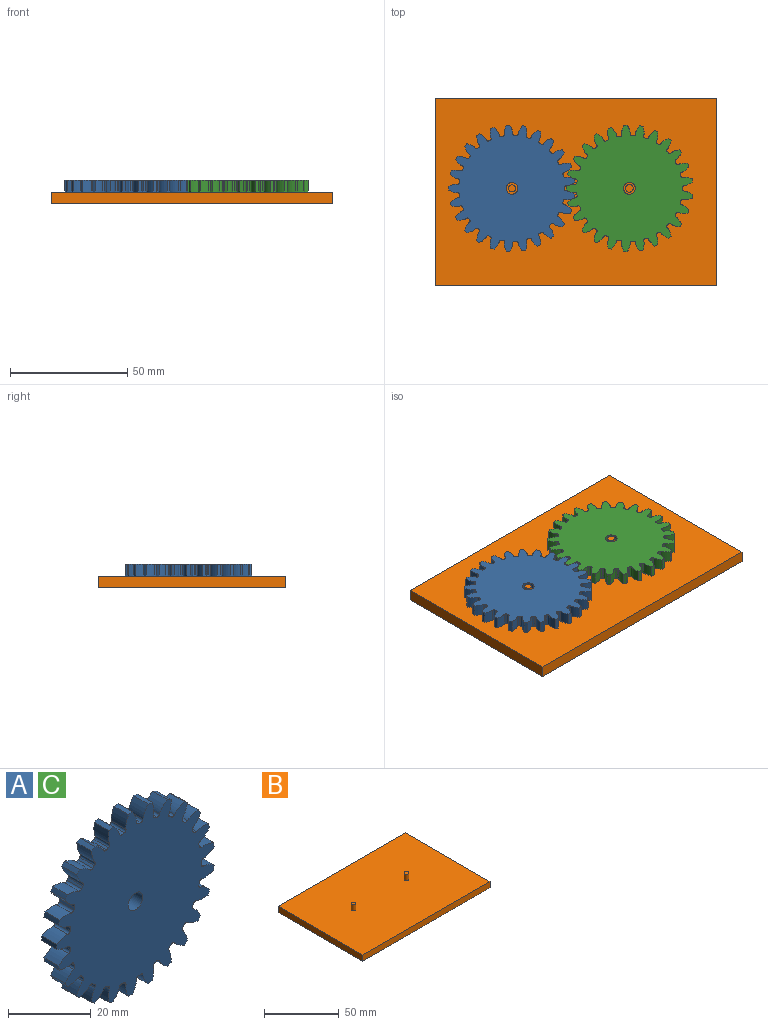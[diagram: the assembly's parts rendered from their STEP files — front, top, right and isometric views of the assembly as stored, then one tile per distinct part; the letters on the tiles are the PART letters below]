
ASSEMBLY  parts=3 mates=2
PART A: 153 faces, bbox 53.9x5x54 mm
  f0: extruded ~5x3.69mm, area 20.3mm2, adj f100,f101,f102,f103
  f1: cylinder r=22.5mm len=5mm, axis (0,1,0), area 3.8mm2, adj f101,f102,f103,f104
  f2: extruded ~5x3.69mm, area 20.3mm2, adj f3,f101,f102,f104
  f3: cylinder r=27mm len=5mm, axis (0,1,0), area 7.2mm2, adj f2,f4,f101,f102
  f4: extruded ~5x3.96mm, area 20.3mm2, adj f3,f101,f102,f105
  f5: cylinder r=22.5mm len=5mm, axis (0,1,0), area 3.8mm2, adj f101,f102,f105,f106
  f6: extruded ~5x3.18mm, area 20.3mm2, adj f7,f101,f102,f106
  f7: cylinder r=27mm len=5mm, axis (0,1,0), area 7.2mm2, adj f6,f8,f101,f102
  f8: extruded ~5x3.98mm, area 20.3mm2, adj f7,f101,f102,f107
  f9: cylinder r=22.5mm len=5mm, axis (0,1,0), area 3.8mm2, adj f101,f102,f107,f108
  f10: extruded ~5x3.14mm, area 20.3mm2, adj f11,f101,f102,f108
  f11: cylinder r=27mm len=5mm, axis (0,1,0), area 7.2mm2, adj f10,f12,f101,f102
  f12: extruded ~5x3.76mm, area 20.3mm2, adj f11,f101,f102,f109
  f13: cylinder r=22.5mm len=5mm, axis (0,1,0), area 3.8mm2, adj f101,f102,f109,f110
  f14: extruded ~5x3.66mm, area 20.3mm2, adj f15,f101,f102,f110
  f15: cylinder r=27mm len=5mm, axis (0,1,0), area 7.2mm2, adj f14,f16,f101,f102
  f16: extruded ~5x3.29mm, area 20.3mm2, adj f15,f101,f102,f111
  f17: cylinder r=22.5mm len=5mm, axis (0,1,0), area 3.8mm2, adj f101,f102,f111,f112
  f18: extruded ~5x3.95mm, area 20.3mm2, adj f19,f101,f102,f112
  f19: cylinder r=27mm len=5mm, axis (0,1,0), area 7.2mm2, adj f18,f20,f101,f102
  f20: extruded ~5x3.03mm, area 20.3mm2, adj f19,f101,f102,f113
  f21: cylinder r=22.5mm len=5mm, axis (0,1,0), area 3.8mm2, adj f101,f102,f113,f114
  f22: extruded ~5x3.99mm, area 20.3mm2, adj f23,f101,f102,f114
  f23: cylinder r=27mm len=5mm, axis (0,1,0), area 7.2mm2, adj f22,f24,f101,f102
  f24: extruded ~5x3.58mm, area 20.3mm2, adj f23,f101,f102,f115
  f25: cylinder r=22.5mm len=5mm, axis (0,1,0), area 3.8mm2, adj f101,f102,f115,f116
  f26: extruded ~5x3.78mm, area 20.3mm2, adj f27,f101,f102,f116
  f27: cylinder r=27mm len=5mm, axis (0,1,0), area 7.2mm2, adj f26,f28,f101,f102
  f28: extruded ~5x3.91mm, area 20.3mm2, adj f27,f101,f102,f117
  f29: cylinder r=22.5mm len=5mm, axis (0,1,0), area 3.8mm2, adj f101,f102,f117,f118
  f30: extruded ~5x3.33mm, area 20.3mm2, adj f31,f101,f102,f118
  f31: cylinder r=27mm len=5mm, axis (0,1,0), area 7.2mm2, adj f30,f32,f101,f102
  f32: extruded ~5x4mm, area 20.3mm2, adj f31,f101,f102,f119
  f33: cylinder r=22.5mm len=5mm, axis (0,1,0), area 3.8mm2, adj f101,f102,f119,f120
  f34: extruded ~5x2.98mm, area 20.3mm2, adj f35,f101,f102,f120
  f35: cylinder r=27mm len=5mm, axis (0,1,0), area 7.2mm2, adj f34,f36,f101,f102
  f36: extruded ~5x3.84mm, area 20.3mm2, adj f35,f101,f102,f121
  f37: cylinder r=22.5mm len=5mm, axis (0,1,0), area 3.8mm2, adj f101,f102,f121,f122
  f38: extruded ~5x3.55mm, area 20.3mm2, adj f39,f101,f102,f122
  f39: cylinder r=27mm len=5mm, axis (0,1,0), area 7.2mm2, adj f38,f40,f101,f102
  f40: extruded ~5x3.43mm, area 20.3mm2, adj f39,f101,f102,f123
  f41: cylinder r=22.5mm len=5mm, axis (0,1,0), area 3.8mm2, adj f101,f102,f123,f124
  f42: extruded ~5x3.9mm, area 20.3mm2, adj f43,f101,f102,f124
  f43: cylinder r=27mm len=5mm, axis (0,1,0), area 7.2mm2, adj f42,f44,f101,f102
  f44: extruded ~5x2.85mm, area 20.3mm2, adj f43,f101,f102,f125
  f45: cylinder r=22.5mm len=5mm, axis (0,1,0), area 3.8mm2, adj f101,f102,f125,f126
  f46: extruded ~5x4mm, area 20.3mm2, adj f47,f101,f102,f126
  f47: cylinder r=27mm len=5mm, axis (0,1,0), area 7.2mm2, adj f46,f48,f101,f102
  f48: extruded ~5x3.46mm, area 20.3mm2, adj f47,f101,f102,f127
  f49: cylinder r=22.5mm len=5mm, axis (0,1,0), area 3.8mm2, adj f101,f102,f127,f128
  f50: extruded ~5x3.85mm, area 20.3mm2, adj f51,f101,f102,f128
  f51: cylinder r=27mm len=5mm, axis (0,1,0), area 7.2mm2, adj f50,f52,f101,f102
  f52: extruded ~5x3.85mm, area 20.3mm2, adj f51,f101,f102,f129
  f53: cylinder r=22.5mm len=5mm, axis (0,1,0), area 3.8mm2, adj f101,f102,f129,f130
  f54: extruded ~5x3.46mm, area 20.3mm2, adj f55,f101,f102,f130
  f55: cylinder r=27mm len=5mm, axis (0,1,0), area 7.2mm2, adj f54,f56,f101,f102
  f56: extruded ~5x4mm, area 20.3mm2, adj f55,f101,f102,f131
  f57: cylinder r=22.5mm len=5mm, axis (0,1,0), area 3.8mm2, adj f101,f102,f131,f132
  f58: extruded ~5x2.85mm, area 20.3mm2, adj f59,f101,f102,f132
  f59: cylinder r=27mm len=5mm, axis (0,1,0), area 7.2mm2, adj f58,f60,f101,f102
  f60: extruded ~5x3.9mm, area 20.3mm2, adj f59,f101,f102,f133
  f61: cylinder r=22.5mm len=5mm, axis (0,1,0), area 3.8mm2, adj f101,f102,f133,f134
  f62: extruded ~5x3.43mm, area 20.3mm2, adj f63,f101,f102,f134
  f63: cylinder r=27mm len=5mm, axis (0,1,0), area 7.2mm2, adj f62,f64,f101,f102
  f64: extruded ~5x3.55mm, area 20.3mm2, adj f63,f101,f102,f135
  f65: cylinder r=22.5mm len=5mm, axis (0,1,0), area 3.8mm2, adj f101,f102,f135,f136
  f66: extruded ~5x3.84mm, area 20.3mm2, adj f67,f101,f102,f136
  f67: cylinder r=27mm len=5mm, axis (0,1,0), area 7.2mm2, adj f66,f68,f101,f102
  f68: extruded ~5x2.98mm, area 20.3mm2, adj f67,f101,f102,f137
  f69: cylinder r=22.5mm len=5mm, axis (0,1,0), area 3.8mm2, adj f101,f102,f137,f138
  f70: extruded ~5x4mm, area 20.3mm2, adj f71,f101,f102,f138
  f71: cylinder r=27mm len=5mm, axis (0,1,0), area 7.2mm2, adj f70,f72,f101,f102
  f72: extruded ~5x3.33mm, area 20.3mm2, adj f71,f101,f102,f139
  f73: cylinder r=22.5mm len=5mm, axis (0,1,0), area 3.8mm2, adj f101,f102,f139,f140
  f74: extruded ~5x3.91mm, area 20.3mm2, adj f75,f101,f102,f140
  f75: cylinder r=27mm len=5mm, axis (0,1,0), area 7.2mm2, adj f74,f76,f101,f102
  f76: extruded ~5x3.78mm, area 20.3mm2, adj f75,f101,f102,f141
  f77: cylinder r=22.5mm len=5mm, axis (0,1,0), area 3.8mm2, adj f101,f102,f141,f142
  f78: extruded ~5x3.58mm, area 20.3mm2, adj f79,f101,f102,f142
  f79: cylinder r=27mm len=5mm, axis (0,1,0), area 7.2mm2, adj f78,f80,f101,f102
  f80: extruded ~5x3.99mm, area 20.3mm2, adj f79,f101,f102,f143
  f81: cylinder r=22.5mm len=5mm, axis (0,1,0), area 3.8mm2, adj f101,f102,f143,f144
  f82: extruded ~5x3.03mm, area 20.3mm2, adj f83,f101,f102,f144
  f83: cylinder r=27mm len=5mm, axis (0,1,0), area 7.2mm2, adj f82,f84,f101,f102
  f84: extruded ~5x3.95mm, area 20.3mm2, adj f83,f101,f102,f145
  f85: cylinder r=22.5mm len=5mm, axis (0,1,0), area 3.8mm2, adj f101,f102,f145,f146
  f86: extruded ~5x3.29mm, area 20.3mm2, adj f87,f101,f102,f146
  f87: cylinder r=27mm len=5mm, axis (0,1,0), area 7.2mm2, adj f86,f88,f101,f102
  f88: extruded ~5x3.66mm, area 20.3mm2, adj f87,f101,f102,f147
  f89: cylinder r=22.5mm len=5mm, axis (0,1,0), area 3.8mm2, adj f101,f102,f147,f148
  f90: extruded ~5x3.76mm, area 20.3mm2, adj f91,f101,f102,f148
  f91: cylinder r=27mm len=5mm, axis (0,1,0), area 7.2mm2, adj f90,f92,f101,f102
  f92: extruded ~5x3.14mm, area 20.3mm2, adj f91,f101,f102,f149
  f93: cylinder r=22.5mm len=5mm, axis (0,1,0), area 3.8mm2, adj f101,f102,f149,f150
  f94: extruded ~5x3.98mm, area 20.3mm2, adj f95,f101,f102,f150
  f95: cylinder r=27mm len=5mm, axis (0,1,0), area 7.2mm2, adj f94,f96,f101,f102
  f96: extruded ~5x3.18mm, area 20.3mm2, adj f95,f101,f102,f151
  f97: cylinder r=22.5mm len=5mm, axis (0,1,0), area 3.8mm2, adj f101,f102,f151,f152
  f98: extruded ~5x3.96mm, area 20.3mm2, adj f100,f101,f102,f152
  f99: cylinder r=2.5mm len=5mm, axis (0,1,0), area 78.5mm2, adj f101,f102
  f100: cylinder r=27mm len=5mm, axis (0,1,0), area 7.2mm2, adj f0,f98,f101,f102
  f101: plane 53.98x53.87mm, normal (0,-1,0), area 1914.3mm2, adj f0,f1,f2,f3,f4,f5,f6,f7
  f102: plane 53.98x53.87mm, normal (0,1,0), area 1914.3mm2, adj f0,f1,f2,f3,f4,f5,f6,f7
  f103: cylinder r=0.72mm len=5mm, axis (0,1,0), area 5.5mm2, adj f0,f1,f101,f102
  f104: cylinder r=0.72mm len=5mm, axis (0,1,0), area 5.5mm2, adj f1,f2,f101,f102
  f105: cylinder r=0.72mm len=5mm, axis (0,1,0), area 5.5mm2, adj f4,f5,f101,f102
  f106: cylinder r=0.72mm len=5mm, axis (0,1,0), area 5.5mm2, adj f5,f6,f101,f102
  f107: cylinder r=0.72mm len=5mm, axis (0,1,0), area 5.5mm2, adj f8,f9,f101,f102
  f108: cylinder r=0.72mm len=5mm, axis (0,1,0), area 5.5mm2, adj f9,f10,f101,f102
  f109: cylinder r=0.72mm len=5mm, axis (0,1,0), area 5.5mm2, adj f12,f13,f101,f102
  f110: cylinder r=0.72mm len=5mm, axis (0,1,0), area 5.5mm2, adj f13,f14,f101,f102
  f111: cylinder r=0.72mm len=5mm, axis (0,1,0), area 5.5mm2, adj f16,f17,f101,f102
  f112: cylinder r=0.72mm len=5mm, axis (0,1,0), area 5.5mm2, adj f17,f18,f101,f102
  f113: cylinder r=0.72mm len=5mm, axis (0,1,0), area 5.5mm2, adj f20,f21,f101,f102
  f114: cylinder r=0.72mm len=5mm, axis (0,1,0), area 5.5mm2, adj f21,f22,f101,f102
  f115: cylinder r=0.72mm len=5mm, axis (0,1,0), area 5.5mm2, adj f24,f25,f101,f102
  f116: cylinder r=0.72mm len=5mm, axis (0,1,0), area 5.5mm2, adj f25,f26,f101,f102
  f117: cylinder r=0.72mm len=5mm, axis (0,1,0), area 5.5mm2, adj f28,f29,f101,f102
  f118: cylinder r=0.72mm len=5mm, axis (0,1,0), area 5.5mm2, adj f29,f30,f101,f102
  f119: cylinder r=0.72mm len=5mm, axis (0,1,0), area 5.5mm2, adj f32,f33,f101,f102
  f120: cylinder r=0.72mm len=5mm, axis (0,1,0), area 5.5mm2, adj f33,f34,f101,f102
  f121: cylinder r=0.72mm len=5mm, axis (0,1,0), area 5.5mm2, adj f36,f37,f101,f102
  f122: cylinder r=0.72mm len=5mm, axis (0,1,0), area 5.5mm2, adj f37,f38,f101,f102
  f123: cylinder r=0.72mm len=5mm, axis (0,1,0), area 5.5mm2, adj f40,f41,f101,f102
  f124: cylinder r=0.72mm len=5mm, axis (0,1,0), area 5.5mm2, adj f41,f42,f101,f102
  f125: cylinder r=0.72mm len=5mm, axis (0,1,0), area 5.5mm2, adj f44,f45,f101,f102
  f126: cylinder r=0.72mm len=5mm, axis (0,1,0), area 5.5mm2, adj f45,f46,f101,f102
  f127: cylinder r=0.72mm len=5mm, axis (0,1,0), area 5.5mm2, adj f48,f49,f101,f102
  f128: cylinder r=0.72mm len=5mm, axis (0,1,0), area 5.5mm2, adj f49,f50,f101,f102
  f129: cylinder r=0.72mm len=5mm, axis (0,1,0), area 5.5mm2, adj f52,f53,f101,f102
  f130: cylinder r=0.72mm len=5mm, axis (0,1,0), area 5.5mm2, adj f53,f54,f101,f102
  f131: cylinder r=0.72mm len=5mm, axis (0,1,0), area 5.5mm2, adj f56,f57,f101,f102
  f132: cylinder r=0.72mm len=5mm, axis (0,1,0), area 5.5mm2, adj f57,f58,f101,f102
  f133: cylinder r=0.72mm len=5mm, axis (0,1,0), area 5.5mm2, adj f60,f61,f101,f102
  f134: cylinder r=0.72mm len=5mm, axis (0,1,0), area 5.5mm2, adj f61,f62,f101,f102
  f135: cylinder r=0.72mm len=5mm, axis (0,1,0), area 5.5mm2, adj f64,f65,f101,f102
  f136: cylinder r=0.72mm len=5mm, axis (0,1,0), area 5.5mm2, adj f65,f66,f101,f102
  f137: cylinder r=0.72mm len=5mm, axis (0,1,0), area 5.5mm2, adj f68,f69,f101,f102
  f138: cylinder r=0.72mm len=5mm, axis (0,1,0), area 5.5mm2, adj f69,f70,f101,f102
  f139: cylinder r=0.72mm len=5mm, axis (0,1,0), area 5.5mm2, adj f72,f73,f101,f102
  f140: cylinder r=0.72mm len=5mm, axis (0,1,0), area 5.5mm2, adj f73,f74,f101,f102
  f141: cylinder r=0.72mm len=5mm, axis (0,1,0), area 5.5mm2, adj f76,f77,f101,f102
  f142: cylinder r=0.72mm len=5mm, axis (0,1,0), area 5.5mm2, adj f77,f78,f101,f102
  f143: cylinder r=0.72mm len=5mm, axis (0,1,0), area 5.5mm2, adj f80,f81,f101,f102
  f144: cylinder r=0.72mm len=5mm, axis (0,1,0), area 5.5mm2, adj f81,f82,f101,f102
  f145: cylinder r=0.72mm len=5mm, axis (0,1,0), area 5.5mm2, adj f84,f85,f101,f102
  f146: cylinder r=0.72mm len=5mm, axis (0,1,0), area 5.5mm2, adj f85,f86,f101,f102
  f147: cylinder r=0.72mm len=5mm, axis (0,1,0), area 5.5mm2, adj f88,f89,f101,f102
  f148: cylinder r=0.72mm len=5mm, axis (0,1,0), area 5.5mm2, adj f89,f90,f101,f102
  f149: cylinder r=0.72mm len=5mm, axis (0,1,0), area 5.5mm2, adj f92,f93,f101,f102
  f150: cylinder r=0.72mm len=5mm, axis (0,1,0), area 5.5mm2, adj f93,f94,f101,f102
  f151: cylinder r=0.72mm len=5mm, axis (0,1,0), area 5.5mm2, adj f96,f97,f101,f102
  f152: cylinder r=0.72mm len=5mm, axis (0,1,0), area 5.5mm2, adj f97,f98,f101,f102
PART B: 10 faces, bbox 120x80x10 mm
  f0: plane 80x5mm, normal (-1,0,0), area 400mm2, adj f1,f3,f4,f5
  f1: plane 120x5mm, normal (0,-1,0), area 600mm2, adj f0,f2,f4,f5
  f2: plane 80x5mm, normal (1,0,0), area 400mm2, adj f1,f3,f4,f5
  f3: plane 120x5mm, normal (0,1,0), area 600mm2, adj f0,f2,f4,f5
  f4: plane 120x80mm, normal (0,0,1), area 9584.5mm2, adj f0,f1,f2,f3,f6,f8
  f5: plane 120x80mm, normal (0,0,-1), area 9600mm2, adj f0,f1,f2,f3
  f6: cylinder r=1.5mm len=5mm, axis (0,0,-1), area 47.1mm2, adj f4,f7
  f7: plane 3x3mm, normal (0,0,1), area 7.1mm2, adj f6
  f8: cylinder r=1.64mm len=5mm, axis (0,0,-1), area 51.4mm2, adj f4,f9
  f9: plane 3.27x3.27mm, normal (0,0,1), area 8.4mm2, adj f8
PART C: same geometry as A
PLACE A rot(axis=(-1,0,0),90deg) t=(-165.23,-79.86,-2.61)mm
PLACE B t=(53.95,39.94,-7.61)mm
PLACE C rot(axis=(-1,0,0),90deg) t=(-115.23,-79.86,-2.61)mm
MATE revolute C.f3 <-> B.f8  axis (0,0,1) through (-115.23,-79.86,2.39)mm
MATE revolute A.f3 <-> B.f6  axis (0,0,1) through (-165.23,-79.86,2.39)mm
